# Revit family: Mieszacz_wody_mechaniczny_podumywalkowy
name_source: partatom
category: Pipe Accessories
units: mm (PartAtom-declared; Revit-internal decimal feet)

## family parameters
Cut with Voids When Loaded = No
Host = Face
Part Type = Normal
Round Connector Dimension = Use Diameter
Shared = No

## types (1)
- FAN9020
    Default Elevation = 1219 mm
    Depth / Glebokosc = 20 mm  [stored 0.0656168 ft]
    Description = Cechy:
- Wysoka odporność na akty wandalizmu dzięki wykonaniu z najwyższej jakości materiałów
- Łatwy montaż
    Height / Wysokosc = 68 mm
    Manufacturer = faneco.com
    Manufacturer code / Kod producenta = 5901764296904
    Material finish / Wykonczenie = Mosiądz pokryty chromem
    Product code / Kod produktu = FAN9020
    Type Comments = Mieszacz wody mechaniczny, podumywalkowy
    URL = https://faneco.com
    Weight / Waga = 0.18 kg
    Width / Szerokosc = 56 mm  [stored 0.183727 ft]

note: [stored X ft] marks values corroborated as IEEE doubles in the binary element streams (Revit-internal decimal feet)

## geometry (parser evidence)
native form markers: Blend x2, Sweep x9
no freeform markers — native parametric forms only
